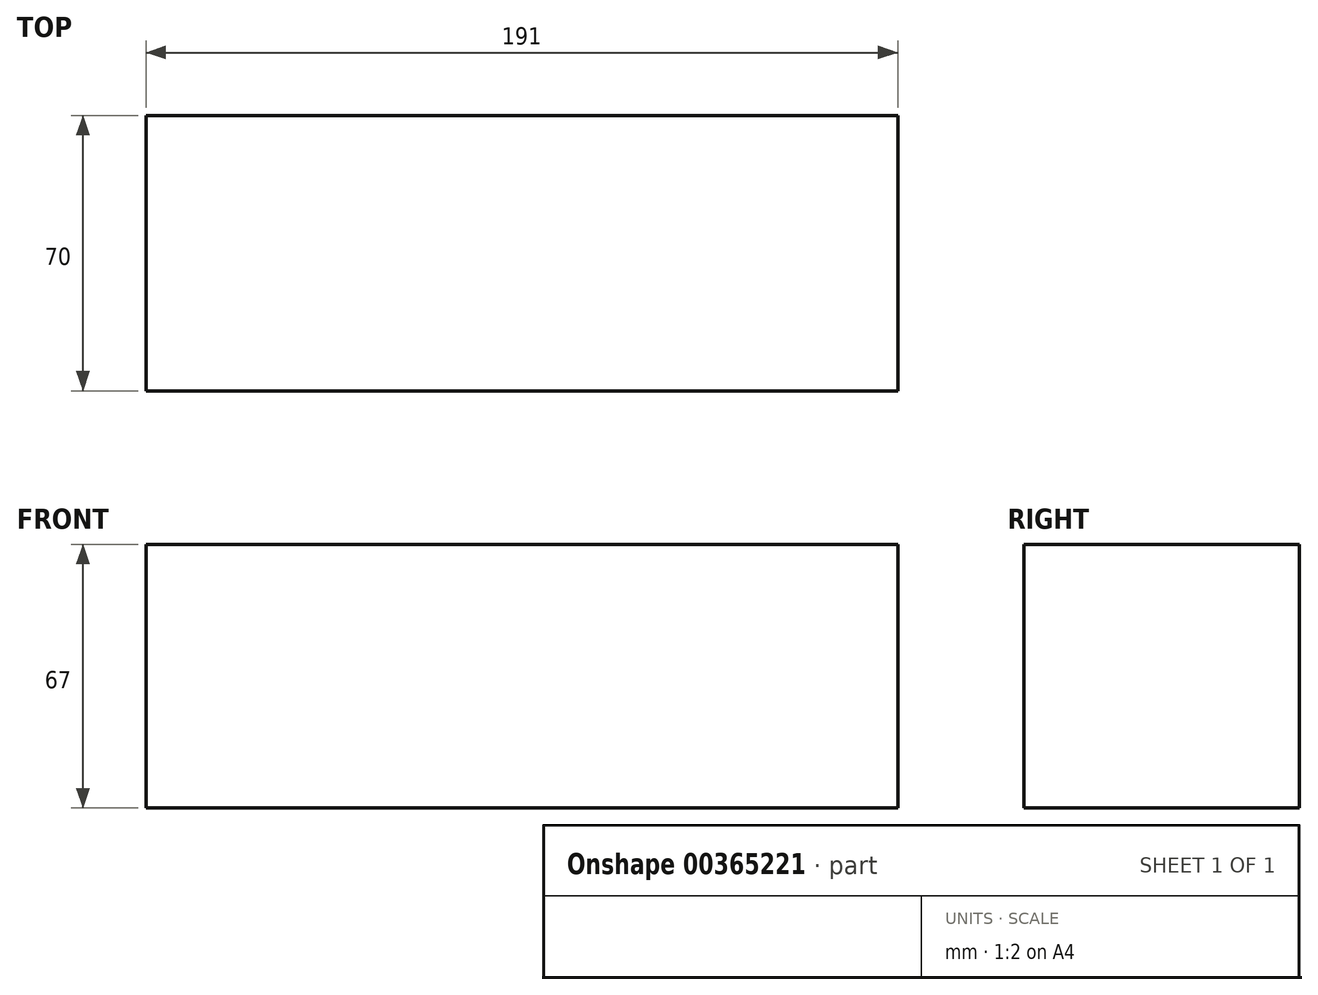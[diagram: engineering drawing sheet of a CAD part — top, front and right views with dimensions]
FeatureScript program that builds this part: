
annotation { "Feature Type Name" : "Feature", "Feature Type Description" : "" }
export const myFeature = defineFeature(function(context is Context, id is Id, definition is map)
    precondition{}
    {
        {
            var Q0;
            Q0=qCreatedBy(makeId("Front.planeOp"),FACE);
            var sketch = newSketch(context, id + "F0", { "sketchPlane" : qUnion([Q0])});
            skLineSegment(sketch, "E0.bottom", {"start": v(95.5, -33.5) * mm, "end": v(-95.5, -33.5) * mm});
            skLineSegment(sketch, "E0.top", {"start": v(95.5, 33.5) * mm, "end": v(-95.5, 33.5) * mm});
            skLineSegment(sketch, "E0.left", {"start": v(95.5, -33.5) * mm, "end": v(95.5, 33.5) * mm});
            skLineSegment(sketch, "E0.right", {"start": v(-95.5, -33.5) * mm, "end": v(-95.5, 33.5) * mm});
            skPoint(sketch, "E0.middle", {"position": v(0, 0) * mm});
            skSolve(sketch);
        }
        {
            var Q0;
            Q0 = qSketchRegion(id + "F0", true);
            extrude(context, id + "F1", {"entities" : qUnion([Q0]), "depth" : 70 * mm});
        }
    });
